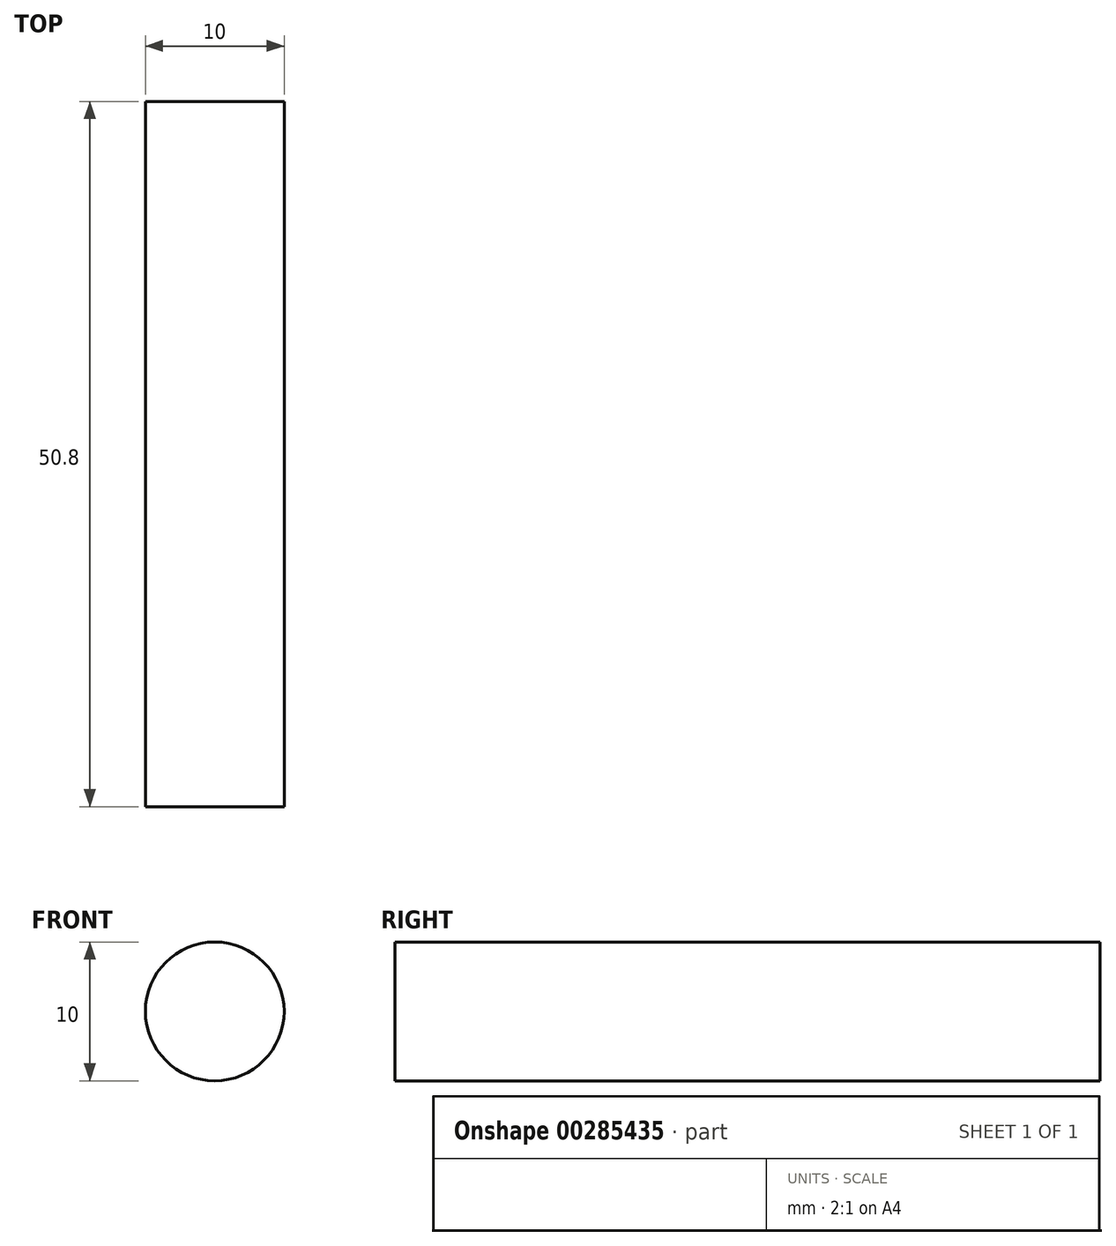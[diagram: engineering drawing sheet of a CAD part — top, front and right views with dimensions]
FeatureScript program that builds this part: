
annotation { "Feature Type Name" : "Feature", "Feature Type Description" : "" }
export const myFeature = defineFeature(function(context is Context, id is Id, definition is map)
    precondition{}
    {
        {
            var Q0;
            Q0=qCreatedBy(makeId("Front.planeOp"),FACE);
            var sketch = newSketch(context, id + "F0", { "sketchPlane" : qUnion([Q0])});
            skCircle(sketch, "E0", {"center": v(0, 0) * mm, "radius": 5 * mm});
            skSolve(sketch);
        }
        {
            var Q0;
            Q0 = qSketchRegion(id + "F0", true);
            extrude(context, id + "F1", {"entities" : qUnion([Q0]), "depth" : 50.8 * mm});
        }
    });
